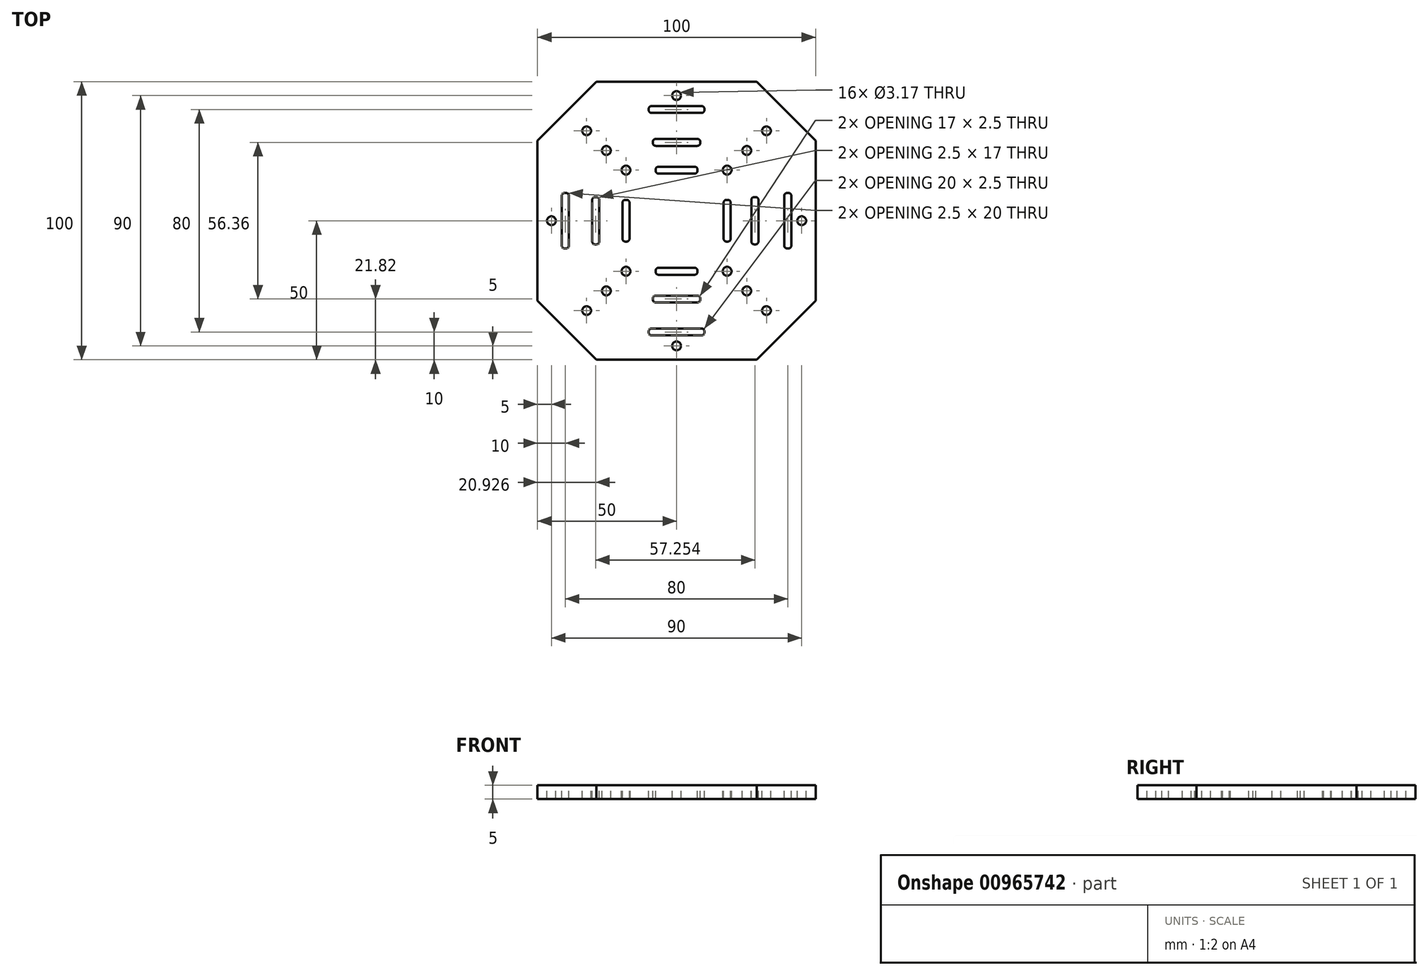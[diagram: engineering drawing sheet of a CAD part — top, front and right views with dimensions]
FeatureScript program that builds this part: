
annotation { "Feature Type Name" : "Feature", "Feature Type Description" : "" }
export const myFeature = defineFeature(function(context is Context, id is Id, definition is map)
    precondition{}
    {
        {
            var Q0;
            Q0=qCreatedBy(makeId("Top.planeOp"),FACE);
            var sketch = newSketch(context, id + "F0", { "sketchPlane" : qUnion([Q0])});
            skLineSegment(sketch, "E0.bottom", {"start": v(50, 50) * mm, "end": v(-50, 50) * mm});
            skLineSegment(sketch, "E0.top", {"start": v(50, -50) * mm, "end": v(-50, -50) * mm});
            skLineSegment(sketch, "E0.left", {"start": v(50, 50) * mm, "end": v(50, -50) * mm});
            skLineSegment(sketch, "E0.right", {"start": v(-50, 50) * mm, "end": v(-50, -50) * mm});
            skPoint(sketch, "E0.middle", {"position": v(0, 0) * mm});
            skSolve(sketch);
        }
        {
            var Q0;
            Q0=qSketchRegion(id+"F0",true);
            extrude(context, id + "F1", {"entities" : qUnion([Q0]), "depth" : 5 * mm, "offsetDistance" : 25 * mm});
        }
        {
            var Q0;
            Q0=makeQuery(id+"F1.opExtrude","SWEPT_EDGE",EDGE,{"disambiguationData":[OSD([sQuery(id+"F0.wireOp",EDGE,"E0.top"),sQuery(id+"F0.wireOp",EDGE,"E0.left")])]});
            var Q1;
            Q1=makeQuery(id+"F1.opExtrude","SWEPT_EDGE",EDGE,{"disambiguationData":[OSD([sQuery(id+"F0.wireOp",EDGE,"E0.bottom"),sQuery(id+"F0.wireOp",EDGE,"E0.left")])]});
            var Q2;
            Q2=makeQuery(id+"F1.opExtrude","SWEPT_EDGE",EDGE,{"disambiguationData":[OSD([sQuery(id+"F0.wireOp",EDGE,"E0.top"),sQuery(id+"F0.wireOp",EDGE,"E0.right")])]});
            var Q3;
            Q3=makeQuery(id+"F1.opExtrude","SWEPT_EDGE",EDGE,{"disambiguationData":[OSD([sQuery(id+"F0.wireOp",EDGE,"E0.bottom"),sQuery(id+"F0.wireOp",EDGE,"E0.right")])]});
            chamfer(context, id + "F2", {"entities" : qUnion([Q0, Q1, Q2, Q3]), "chamferType" : ChamferType.OFFSET_ANGLE, "width" : 21.21 * mm, "oppositeDirection" : false, "angle" : 45 * degree, "tangentPropagation" : true});
        }
        {
            var Q0;
            Q0=makeQuery(id+"F1.opExtrude","CAP_FACE",FACE,{"disambiguationData":[OSD([sQuery(id+"F0.wireOp",EDGE,"E0.bottom"),sQuery(id+"F0.wireOp",EDGE,"E0.top"),sQuery(id+"F0.wireOp",EDGE,"E0.left"),sQuery(id+"F0.wireOp",EDGE,"E0.right")])],"isStart":false});
            var sketch = newSketch(context, id + "F3", { "sketchPlane" : qUnion([Q0])});
            skLineSegment(sketch, "E1", {"start": v(-50, 28.79) * mm, "end": v(-14.64, -6.57) * mm});
            skLineSegment(sketch, "E2", {"start": v(-14.64, -6.57) * mm, "end": v(6.57, 14.64) * mm});
            skLineSegment(sketch, "E3", {"start": v(6.57, 14.64) * mm, "end": v(-28.79, 50) * mm});
            skCircle(sketch, "E4", {"center": v(-25.25, 25.25) * mm, "radius": 1.59 * mm});
            skLineSegment(sketch, "E5", {"start": v(-28.79, -50) * mm, "end": v(-0.5, -21.72) * mm});
            skLineSegment(sketch, "E6", {"start": v(-0.5, -21.72) * mm, "end": v(-21.72, -0.5) * mm});
            skLineSegment(sketch, "E7", {"start": v(-21.72, -0.5) * mm, "end": v(-50, -28.79) * mm});
            skLineSegment(sketch, "E8", {"start": v(50, -28.79) * mm, "end": v(14.64, 6.57) * mm});
            skLineSegment(sketch, "E9", {"start": v(14.64, 6.57) * mm, "end": v(-6.57, -14.64) * mm});
            skLineSegment(sketch, "E10", {"start": v(-6.57, -14.64) * mm, "end": v(28.79, -50) * mm});
            skLineSegment(sketch, "E11", {"start": v(28.79, 50) * mm, "end": v(0.5, 21.72) * mm});
            skLineSegment(sketch, "E12", {"start": v(0.5, 21.72) * mm, "end": v(21.72, 0.5) * mm});
            skLineSegment(sketch, "E13", {"start": v(21.72, 0.5) * mm, "end": v(50, 28.79) * mm});
            skCircle(sketch, "E14", {"center": v(-25.25, -25.25) * mm, "radius": 1.59 * mm});
            skCircle(sketch, "E15", {"center": v(25.25, -25.25) * mm, "radius": 1.59 * mm});
            skCircle(sketch, "E16", {"center": v(25.25, 25.25) * mm, "radius": 1.59 * mm});
            skCircle(sketch, "E17", {"center": v(-18.18, -18.18) * mm, "radius": 1.59 * mm});
            skCircle(sketch, "E18", {"center": v(18.18, -18.18) * mm, "radius": 1.59 * mm});
            skCircle(sketch, "E19", {"center": v(18.18, 18.18) * mm, "radius": 1.59 * mm});
            skCircle(sketch, "E20", {"center": v(-18.18, 18.18) * mm, "radius": 1.59 * mm});
            skCircle(sketch, "E21", {"center": v(-32.32, 32.32) * mm, "radius": 1.59 * mm});
            skCircle(sketch, "E22", {"center": v(-32.32, -32.32) * mm, "radius": 1.59 * mm});
            skCircle(sketch, "E23", {"center": v(32.32, -32.32) * mm, "radius": 1.59 * mm});
            skCircle(sketch, "E24", {"center": v(32.32, 32.32) * mm, "radius": 1.59 * mm});
            skPoint(sketch, "E25.middle", {"position": v(0, 40) * mm});
            skLineSegment(sketch, "E26.bottom", {"start": v(41.25, -10) * mm, "end": v(38.75, -10) * mm});
            skLineSegment(sketch, "E26.top", {"start": v(41.25, 10) * mm, "end": v(38.75, 10) * mm});
            skLineSegment(sketch, "E26.left", {"start": v(41.25, -10) * mm, "end": v(41.25, 10) * mm});
            skLineSegment(sketch, "E26.right", {"start": v(38.75, -10) * mm, "end": v(38.75, 10) * mm});
            skPoint(sketch, "E26.middle", {"position": v(40, 0) * mm});
            skLineSegment(sketch, "E27.bottom", {"start": v(-38.75, 10) * mm, "end": v(-41.25, 10) * mm});
            skLineSegment(sketch, "E27.top", {"start": v(-38.75, -10) * mm, "end": v(-41.25, -10) * mm});
            skLineSegment(sketch, "E27.left", {"start": v(-38.75, 10) * mm, "end": v(-38.75, -10) * mm});
            skLineSegment(sketch, "E27.right", {"start": v(-41.25, 10) * mm, "end": v(-41.25, -10) * mm});
            skPoint(sketch, "E27.middle", {"position": v(-40, 0) * mm});
            skLineSegment(sketch, "E28.bottom", {"start": v(10, -41.25) * mm, "end": v(-10, -41.25) * mm});
            skLineSegment(sketch, "E28.top", {"start": v(10, -38.75) * mm, "end": v(-10, -38.75) * mm});
            skLineSegment(sketch, "E28.left", {"start": v(10, -41.25) * mm, "end": v(10, -38.75) * mm});
            skLineSegment(sketch, "E28.right", {"start": v(-10, -41.25) * mm, "end": v(-10, -38.75) * mm});
            skPoint(sketch, "E28.middle", {"position": v(0, -40) * mm});
            skLineSegment(sketch, "E29.bottom", {"start": v(10, 41.25) * mm, "end": v(-10, 41.25) * mm});
            skLineSegment(sketch, "E29.top", {"start": v(10, 38.75) * mm, "end": v(-10, 38.75) * mm});
            skLineSegment(sketch, "E29.left", {"start": v(10, 41.25) * mm, "end": v(10, 38.75) * mm});
            skLineSegment(sketch, "E29.right", {"start": v(-10, 41.25) * mm, "end": v(-10, 38.75) * mm});
            skCircle(sketch, "E30", {"center": v(-45, 0) * mm, "radius": 1.59 * mm});
            skCircle(sketch, "E31", {"center": v(0, 45) * mm, "radius": 1.59 * mm});
            skCircle(sketch, "E32", {"center": v(0, -45) * mm, "radius": 1.59 * mm});
            skCircle(sketch, "E33", {"center": v(45, 0) * mm, "radius": 1.59 * mm});
            skSolve(sketch);
        }
        {
            var Q0;
            Q0=makeQuery(id+"F3.imprint","IMPRINT",FACE,{"disambiguationData":[TD([[makeQuery(id+"F3.imprint","IMPRINT",EDGE,{"derivedFrom":sQuery(id+"F3.wireOp",EDGE,"E4")}),1.0]])]});
            var Q1;
            Q1=makeQuery(id+"F3.imprint","IMPRINT",FACE,{"disambiguationData":[TD([[makeQuery(id+"F3.imprint","IMPRINT",EDGE,{"derivedFrom":sQuery(id+"F3.wireOp",EDGE,"E14")}),1.0]])]});
            var Q2;
            Q2=makeQuery(id+"F3.imprint","IMPRINT",FACE,{"disambiguationData":[TD([[makeQuery(id+"F3.imprint","IMPRINT",EDGE,{"derivedFrom":sQuery(id+"F3.wireOp",EDGE,"E15")}),1.0]])]});
            var Q3;
            Q3=makeQuery(id+"F3.imprint","IMPRINT",FACE,{"disambiguationData":[TD([[makeQuery(id+"F3.imprint","IMPRINT",EDGE,{"derivedFrom":sQuery(id+"F3.wireOp",EDGE,"E16")}),1.0]])]});
            var Q4;
            Q4=makeQuery(id+"F3.imprint","IMPRINT",FACE,{"disambiguationData":[TD([[makeQuery(id+"F3.imprint","IMPRINT",EDGE,{"derivedFrom":sQuery(id+"F3.wireOp",EDGE,"E17")}),1.0]])]});
            var Q5;
            Q5=makeQuery(id+"F3.imprint","IMPRINT",FACE,{"disambiguationData":[TD([[makeQuery(id+"F3.imprint","IMPRINT",EDGE,{"derivedFrom":sQuery(id+"F3.wireOp",EDGE,"E18")}),1.0]])]});
            var Q6;
            Q6=makeQuery(id+"F3.imprint","IMPRINT",FACE,{"disambiguationData":[TD([[makeQuery(id+"F3.imprint","IMPRINT",EDGE,{"derivedFrom":sQuery(id+"F3.wireOp",EDGE,"E19")}),1.0]])]});
            var Q7;
            Q7=makeQuery(id+"F3.imprint","IMPRINT",FACE,{"disambiguationData":[TD([[makeQuery(id+"F3.imprint","IMPRINT",EDGE,{"derivedFrom":sQuery(id+"F3.wireOp",EDGE,"E20")}),1.0]])]});
            var Q8;
            Q8=makeQuery(id+"F3.imprint","IMPRINT",FACE,{"disambiguationData":[TD([[makeQuery(id+"F3.imprint","IMPRINT",EDGE,{"derivedFrom":sQuery(id+"F3.wireOp",EDGE,"E22")}),1.0]])]});
            var Q9;
            Q9=makeQuery(id+"F3.imprint","IMPRINT",FACE,{"disambiguationData":[TD([[makeQuery(id+"F3.imprint","IMPRINT",EDGE,{"derivedFrom":sQuery(id+"F3.wireOp",EDGE,"E23")}),1.0]])]});
            var Q10;
            Q10=makeQuery(id+"F3.imprint","IMPRINT",FACE,{"disambiguationData":[TD([[makeQuery(id+"F3.imprint","IMPRINT",EDGE,{"derivedFrom":sQuery(id+"F3.wireOp",EDGE,"E24")}),1.0]])]});
            var Q11;
            Q11=makeQuery(id+"F3.imprint","IMPRINT",FACE,{"disambiguationData":[TD([[makeQuery(id+"F3.imprint","IMPRINT",EDGE,{"derivedFrom":sQuery(id+"F3.wireOp",EDGE,"E21")}),1.0]])]});
            var Q12;
            Q12=makeQuery(id+"F3.imprint","IMPRINT",FACE,{"disambiguationData":[TD([[makeQuery(id+"F3.imprint","IMPRINT",EDGE,{"derivedFrom":sQuery(id+"F3.wireOp",EDGE,"E27.bottom")}),1.0]])]});
            var Q13;
            Q13=makeQuery(id+"F3.imprint","IMPRINT",FACE,{"disambiguationData":[TD([[makeQuery(id+"F3.imprint","IMPRINT",EDGE,{"derivedFrom":sQuery(id+"F3.wireOp",EDGE,"E30")}),1.0]])]});
            var Q14;
            Q14=makeQuery(id+"F3.imprint","IMPRINT",FACE,{"disambiguationData":[TD([[makeQuery(id+"F3.imprint","IMPRINT",EDGE,{"derivedFrom":sQuery(id+"F3.wireOp",EDGE,"E28.bottom")}),-1.0]])]});
            var Q15;
            Q15=makeQuery(id+"F3.imprint","IMPRINT",FACE,{"disambiguationData":[TD([[makeQuery(id+"F3.imprint","IMPRINT",EDGE,{"derivedFrom":sQuery(id+"F3.wireOp",EDGE,"E32")}),1.0]])]});
            var Q16;
            Q16=makeQuery(id+"F3.imprint","IMPRINT",FACE,{"disambiguationData":[TD([[makeQuery(id+"F3.imprint","IMPRINT",EDGE,{"derivedFrom":sQuery(id+"F3.wireOp",EDGE,"E26.bottom")}),-1.0]])]});
            var Q17;
            Q17=makeQuery(id+"F3.imprint","IMPRINT",FACE,{"disambiguationData":[TD([[makeQuery(id+"F3.imprint","IMPRINT",EDGE,{"derivedFrom":sQuery(id+"F3.wireOp",EDGE,"E33")}),1.0]])]});
            var Q18;
            Q18=makeQuery(id+"F3.imprint","IMPRINT",FACE,{"disambiguationData":[TD([[makeQuery(id+"F3.imprint","IMPRINT",EDGE,{"derivedFrom":sQuery(id+"F3.wireOp",EDGE,"E31")}),1.0]])]});
            var Q19;
            Q19=makeQuery(id+"F3.imprint","IMPRINT",FACE,{"disambiguationData":[TD([[makeQuery(id+"F3.imprint","IMPRINT",EDGE,{"derivedFrom":sQuery(id+"F3.wireOp",EDGE,"E29.bottom")}),1.0]])]});
            extrude(context, id + "F4", {"entities" : qUnion([Q0, Q1, Q2, Q3, Q4, Q5, Q6, Q7, Q8, Q9, Q10, Q11, Q12, Q13, Q14, Q15, Q16, Q17, Q18, Q19]), "operationType" : NewBodyOperationType.REMOVE, "oppositeDirection" : true, "depth" : 5 * mm, "offsetDistance" : 25 * mm});
        }
        {
            var Q0;
            Q0=makeQuery(id+"F4.boolean.opBoolean","COPY",EDGE,{"derivedFrom":makeQuery(id+"F4.opExtrude","SWEPT_EDGE",EDGE,{"disambiguationData":[OSD([sQuery(id+"F3.wireOp",EDGE,"E27.bottom"),sQuery(id+"F3.wireOp",EDGE,"E27.right")])]})});
            var Q1;
            Q1=makeQuery(id+"F4.boolean.opBoolean","COPY",EDGE,{"derivedFrom":makeQuery(id+"F4.opExtrude","SWEPT_EDGE",EDGE,{"disambiguationData":[OSD([sQuery(id+"F3.wireOp",EDGE,"E28.top"),sQuery(id+"F3.wireOp",EDGE,"E28.right")])]})});
            var Q2;
            Q2=makeQuery(id+"F4.boolean.opBoolean","COPY",EDGE,{"derivedFrom":makeQuery(id+"F4.opExtrude","SWEPT_EDGE",EDGE,{"disambiguationData":[OSD([sQuery(id+"F3.wireOp",EDGE,"E26.top"),sQuery(id+"F3.wireOp",EDGE,"E26.right")])]})});
            var Q3;
            Q3=makeQuery(id+"F4.boolean.opBoolean","COPY",EDGE,{"derivedFrom":makeQuery(id+"F4.opExtrude","SWEPT_EDGE",EDGE,{"disambiguationData":[OSD([sQuery(id+"F3.wireOp",EDGE,"E29.bottom"),sQuery(id+"F3.wireOp",EDGE,"E29.right")])]})});
            var Q4;
            Q4=makeQuery(id+"F4.boolean.opBoolean","COPY",EDGE,{"derivedFrom":makeQuery(id+"F4.opExtrude","SWEPT_EDGE",EDGE,{"disambiguationData":[OSD([sQuery(id+"F3.wireOp",EDGE,"E28.top"),sQuery(id+"F3.wireOp",EDGE,"E28.left")])]})});
            var Q5;
            Q5=makeQuery(id+"F4.boolean.opBoolean","COPY",EDGE,{"derivedFrom":makeQuery(id+"F4.opExtrude","SWEPT_EDGE",EDGE,{"disambiguationData":[OSD([sQuery(id+"F3.wireOp",EDGE,"E26.top"),sQuery(id+"F3.wireOp",EDGE,"E26.left")])]})});
            var Q6;
            Q6=makeQuery(id+"F4.boolean.opBoolean","COPY",EDGE,{"derivedFrom":makeQuery(id+"F4.opExtrude","SWEPT_EDGE",EDGE,{"disambiguationData":[OSD([sQuery(id+"F3.wireOp",EDGE,"E27.bottom"),sQuery(id+"F3.wireOp",EDGE,"E27.left")])]})});
            var Q7;
            Q7=makeQuery(id+"F4.boolean.opBoolean","COPY",EDGE,{"derivedFrom":makeQuery(id+"F4.opExtrude","SWEPT_EDGE",EDGE,{"disambiguationData":[OSD([sQuery(id+"F3.wireOp",EDGE,"E29.bottom"),sQuery(id+"F3.wireOp",EDGE,"E29.left")])]})});
            var Q8;
            Q8=makeQuery(id+"F4.boolean.opBoolean","COPY",EDGE,{"derivedFrom":makeQuery(id+"F4.opExtrude","SWEPT_EDGE",EDGE,{"disambiguationData":[OSD([sQuery(id+"F3.wireOp",EDGE,"E26.bottom"),sQuery(id+"F3.wireOp",EDGE,"E26.left")])]})});
            var Q9;
            Q9=makeQuery(id+"F4.boolean.opBoolean","COPY",EDGE,{"derivedFrom":makeQuery(id+"F4.opExtrude","SWEPT_EDGE",EDGE,{"disambiguationData":[OSD([sQuery(id+"F3.wireOp",EDGE,"E28.bottom"),sQuery(id+"F3.wireOp",EDGE,"E28.left")])]})});
            var Q10;
            Q10=makeQuery(id+"F4.boolean.opBoolean","COPY",EDGE,{"derivedFrom":makeQuery(id+"F4.opExtrude","SWEPT_EDGE",EDGE,{"disambiguationData":[OSD([sQuery(id+"F3.wireOp",EDGE,"E29.top"),sQuery(id+"F3.wireOp",EDGE,"E29.left")])]})});
            var Q11;
            Q11=makeQuery(id+"F4.boolean.opBoolean","COPY",EDGE,{"derivedFrom":makeQuery(id+"F4.opExtrude","SWEPT_EDGE",EDGE,{"disambiguationData":[OSD([sQuery(id+"F3.wireOp",EDGE,"E27.top"),sQuery(id+"F3.wireOp",EDGE,"E27.left")])]})});
            var Q12;
            Q12=makeQuery(id+"F4.boolean.opBoolean","COPY",EDGE,{"derivedFrom":makeQuery(id+"F4.opExtrude","SWEPT_EDGE",EDGE,{"disambiguationData":[OSD([sQuery(id+"F3.wireOp",EDGE,"E29.top"),sQuery(id+"F3.wireOp",EDGE,"E29.right")])]})});
            var Q13;
            Q13=makeQuery(id+"F4.boolean.opBoolean","COPY",EDGE,{"derivedFrom":makeQuery(id+"F4.opExtrude","SWEPT_EDGE",EDGE,{"disambiguationData":[OSD([sQuery(id+"F3.wireOp",EDGE,"E26.bottom"),sQuery(id+"F3.wireOp",EDGE,"E26.right")])]})});
            var Q14;
            Q14=makeQuery(id+"F4.boolean.opBoolean","COPY",EDGE,{"derivedFrom":makeQuery(id+"F4.opExtrude","SWEPT_EDGE",EDGE,{"disambiguationData":[OSD([sQuery(id+"F3.wireOp",EDGE,"E27.top"),sQuery(id+"F3.wireOp",EDGE,"E27.right")])]})});
            var Q15;
            Q15=makeQuery(id+"F4.boolean.opBoolean","COPY",EDGE,{"derivedFrom":makeQuery(id+"F4.opExtrude","SWEPT_EDGE",EDGE,{"disambiguationData":[OSD([sQuery(id+"F3.wireOp",EDGE,"E28.bottom"),sQuery(id+"F3.wireOp",EDGE,"E28.right")])]})});
            fillet(context, id + "F5", {"entities" : qUnion([Q0, Q1, Q2, Q3, Q4, Q5, Q6, Q7, Q8, Q9, Q10, Q11, Q12, Q13, Q14, Q15]), "radius" : 1 * mm, "tangentPropagation" : true, "allowEdgeOverflow" : false});
        }
        {
            var Q0;
            Q0=makeQuery(id+"F1.opExtrude","CAP_FACE",FACE,{"disambiguationData":[OSD([sQuery(id+"F0.wireOp",EDGE,"E0.bottom"),sQuery(id+"F0.wireOp",EDGE,"E0.top"),sQuery(id+"F0.wireOp",EDGE,"E0.left"),sQuery(id+"F0.wireOp",EDGE,"E0.right")])],"isStart":false});
            var sketch = newSketch(context, id + "F6", { "sketchPlane" : qUnion([Q0])});
            skLineSegment(sketch, "E34", {"start": v(-18.18, 18.18) * mm, "end": v(-7.5, 18.18) * mm});
            skLineSegment(sketch, "E35.bottom", {"start": v(7.5, 19.43) * mm, "end": v(-7.5, 19.43) * mm});
            skLineSegment(sketch, "E35.top", {"start": v(7.5, 16.93) * mm, "end": v(-7.5, 16.93) * mm});
            skLineSegment(sketch, "E35.left", {"start": v(7.5, 19.43) * mm, "end": v(7.5, 16.93) * mm});
            skLineSegment(sketch, "E35.right", {"start": v(-7.5, 19.43) * mm, "end": v(-7.5, 16.93) * mm});
            skPoint(sketch, "E35.middle", {"position": v(0, 18.18) * mm});
            skLineSegment(sketch, "E36.bottom", {"start": v(-19.43, 7.5) * mm, "end": v(-16.93, 7.5) * mm});
            skLineSegment(sketch, "E36.top", {"start": v(-19.43, -7.5) * mm, "end": v(-16.93, -7.5) * mm});
            skLineSegment(sketch, "E36.left", {"start": v(-19.43, 7.5) * mm, "end": v(-19.43, -7.5) * mm});
            skLineSegment(sketch, "E36.right", {"start": v(-16.93, 7.5) * mm, "end": v(-16.93, -7.5) * mm});
            skPoint(sketch, "E36.middle", {"position": v(-18.18, 0) * mm});
            skLineSegment(sketch, "E37.bottom", {"start": v(7.5, -16.93) * mm, "end": v(-7.5, -16.93) * mm});
            skLineSegment(sketch, "E37.top", {"start": v(7.5, -19.43) * mm, "end": v(-7.5, -19.43) * mm});
            skLineSegment(sketch, "E37.left", {"start": v(7.5, -16.93) * mm, "end": v(7.5, -19.43) * mm});
            skLineSegment(sketch, "E37.right", {"start": v(-7.5, -16.93) * mm, "end": v(-7.5, -19.43) * mm});
            skPoint(sketch, "E37.middle", {"position": v(0, -18.18) * mm});
            skLineSegment(sketch, "E38.bottom", {"start": v(19.43, 7.5) * mm, "end": v(16.93, 7.5) * mm});
            skLineSegment(sketch, "E38.top", {"start": v(19.43, -7.5) * mm, "end": v(16.93, -7.5) * mm});
            skLineSegment(sketch, "E38.left", {"start": v(19.43, 7.5) * mm, "end": v(19.43, -7.5) * mm});
            skLineSegment(sketch, "E38.right", {"start": v(16.93, 7.5) * mm, "end": v(16.93, -7.5) * mm});
            skPoint(sketch, "E38.middle", {"position": v(18.18, 0) * mm});
            skLineSegment(sketch, "E39.bottom", {"start": v(-27.82, 8.5) * mm, "end": v(-30.32, 8.5) * mm});
            skLineSegment(sketch, "E39.top", {"start": v(-27.82, -8.5) * mm, "end": v(-30.32, -8.5) * mm});
            skLineSegment(sketch, "E39.left", {"start": v(-27.82, 8.5) * mm, "end": v(-27.82, -8.5) * mm});
            skLineSegment(sketch, "E39.right", {"start": v(-30.32, 8.5) * mm, "end": v(-30.32, -8.5) * mm});
            skPoint(sketch, "E39.middle", {"position": v(-29.07, 0) * mm});
            skLineSegment(sketch, "E40", {"start": v(0, 18.18) * mm, "end": v(0, 19.43) * mm});
            skLineSegment(sketch, "E41", {"start": v(0, -18.18) * mm, "end": v(0, -19.43) * mm});
            skLineSegment(sketch, "E42.bottom", {"start": v(8.5, -26.93) * mm, "end": v(-8.5, -26.93) * mm});
            skLineSegment(sketch, "E42.top", {"start": v(8.5, -29.43) * mm, "end": v(-8.5, -29.43) * mm});
            skLineSegment(sketch, "E42.left", {"start": v(8.5, -26.93) * mm, "end": v(8.5, -29.43) * mm});
            skLineSegment(sketch, "E42.right", {"start": v(-8.5, -26.93) * mm, "end": v(-8.5, -29.43) * mm});
            skPoint(sketch, "E42.middle", {"position": v(0, -28.18) * mm});
            skLineSegment(sketch, "E43.bottom", {"start": v(29.43, 8.5) * mm, "end": v(26.93, 8.5) * mm});
            skLineSegment(sketch, "E43.top", {"start": v(29.43, -8.5) * mm, "end": v(26.93, -8.5) * mm});
            skLineSegment(sketch, "E43.left", {"start": v(29.43, 8.5) * mm, "end": v(29.43, -8.5) * mm});
            skLineSegment(sketch, "E43.right", {"start": v(26.93, 8.5) * mm, "end": v(26.93, -8.5) * mm});
            skPoint(sketch, "E43.middle", {"position": v(28.18, 0) * mm});
            skLineSegment(sketch, "E44.bottom", {"start": v(8.5, 29.43) * mm, "end": v(-8.5, 29.43) * mm});
            skLineSegment(sketch, "E44.top", {"start": v(8.5, 26.93) * mm, "end": v(-8.5, 26.93) * mm});
            skLineSegment(sketch, "E44.left", {"start": v(8.5, 29.43) * mm, "end": v(8.5, 26.93) * mm});
            skLineSegment(sketch, "E44.right", {"start": v(-8.5, 29.43) * mm, "end": v(-8.5, 26.93) * mm});
            skPoint(sketch, "E44.middle", {"position": v(0, 28.18) * mm});
            skLineSegment(sketch, "E45.trimOffspring", {"start": v(-27.82, 0) * mm, "end": v(-29.07, 0) * mm});
            skPoint(sketch, "E46.orphan", {"position": v(-18.18, -18.18) * mm});
            skLineSegment(sketch, "E47.trimOffspring", {"start": v(0, -26.93) * mm, "end": v(0, -28.18) * mm});
            skLineSegment(sketch, "E48.trimOffspring", {"start": v(0, 26.93) * mm, "end": v(0, 28.18) * mm});
            skPoint(sketch, "E49.orphan", {"position": v(18.18, 18.18) * mm});
            skLineSegment(sketch, "E50.trimOffspring", {"start": v(26.93, 0) * mm, "end": v(28.18, 0) * mm});
            skPoint(sketch, "E51.end.orphan", {"position": v(18.18, -18.18) * mm});
            skSolve(sketch);
        }
        {
            var Q0;
            Q0=qSketchRegion(id+"F6",true);
            extrude(context, id + "F7", {"entities" : qUnion([Q0]), "operationType" : NewBodyOperationType.REMOVE, "oppositeDirection" : true, "depth" : 5 * mm, "offsetDistance" : 25 * mm});
        }
        {
            var Q0;
            Q0=makeQuery(id+"F7.boolean.opBoolean","COPY",EDGE,{"derivedFrom":makeQuery(id+"F7.opExtrude","SWEPT_EDGE",EDGE,{"disambiguationData":[OSD([sQuery(id+"F6.wireOp",EDGE,"E39.bottom"),sQuery(id+"F6.wireOp",EDGE,"E39.right")])]})});
            var Q1;
            Q1=makeQuery(id+"F7.boolean.opBoolean","COPY",EDGE,{"derivedFrom":makeQuery(id+"F7.opExtrude","SWEPT_EDGE",EDGE,{"disambiguationData":[OSD([sQuery(id+"F6.wireOp",EDGE,"E36.bottom"),sQuery(id+"F6.wireOp",EDGE,"E36.left")])]})});
            var Q2;
            Q2=makeQuery(id+"F7.boolean.opBoolean","COPY",EDGE,{"derivedFrom":makeQuery(id+"F7.opExtrude","SWEPT_EDGE",EDGE,{"disambiguationData":[OSD([sQuery(id+"F6.wireOp",EDGE,"E44.bottom"),sQuery(id+"F6.wireOp",EDGE,"E44.right")])]})});
            var Q3;
            Q3=makeQuery(id+"F7.boolean.opBoolean","COPY",EDGE,{"derivedFrom":makeQuery(id+"F7.opExtrude","SWEPT_EDGE",EDGE,{"disambiguationData":[OSD([sQuery(id+"F6.wireOp",EDGE,"E35.bottom"),sQuery(id+"F6.wireOp",EDGE,"E35.right")])]})});
            var Q4;
            Q4=makeQuery(id+"F7.boolean.opBoolean","COPY",EDGE,{"derivedFrom":makeQuery(id+"F7.opExtrude","SWEPT_EDGE",EDGE,{"disambiguationData":[OSD([sQuery(id+"F6.wireOp",EDGE,"E37.bottom"),sQuery(id+"F6.wireOp",EDGE,"E37.right")])]})});
            var Q5;
            Q5=makeQuery(id+"F7.boolean.opBoolean","COPY",EDGE,{"derivedFrom":makeQuery(id+"F7.opExtrude","SWEPT_EDGE",EDGE,{"disambiguationData":[OSD([sQuery(id+"F6.wireOp",EDGE,"E42.bottom"),sQuery(id+"F6.wireOp",EDGE,"E42.right")])]})});
            var Q6;
            Q6=makeQuery(id+"F7.boolean.opBoolean","COPY",EDGE,{"derivedFrom":makeQuery(id+"F7.opExtrude","SWEPT_EDGE",EDGE,{"disambiguationData":[OSD([sQuery(id+"F6.wireOp",EDGE,"E38.bottom"),sQuery(id+"F6.wireOp",EDGE,"E38.right")])]})});
            var Q7;
            Q7=makeQuery(id+"F7.boolean.opBoolean","COPY",EDGE,{"derivedFrom":makeQuery(id+"F7.opExtrude","SWEPT_EDGE",EDGE,{"disambiguationData":[OSD([sQuery(id+"F6.wireOp",EDGE,"E43.bottom"),sQuery(id+"F6.wireOp",EDGE,"E43.right")])]})});
            var Q8;
            Q8=makeQuery(id+"F7.boolean.opBoolean","COPY",EDGE,{"derivedFrom":makeQuery(id+"F7.opExtrude","SWEPT_EDGE",EDGE,{"disambiguationData":[OSD([sQuery(id+"F6.wireOp",EDGE,"E44.bottom"),sQuery(id+"F6.wireOp",EDGE,"E44.left")])]})});
            var Q9;
            Q9=makeQuery(id+"F7.boolean.opBoolean","COPY",EDGE,{"derivedFrom":makeQuery(id+"F7.opExtrude","SWEPT_EDGE",EDGE,{"disambiguationData":[OSD([sQuery(id+"F6.wireOp",EDGE,"E35.bottom"),sQuery(id+"F6.wireOp",EDGE,"E35.left")])]})});
            var Q10;
            Q10=makeQuery(id+"F7.boolean.opBoolean","COPY",EDGE,{"derivedFrom":makeQuery(id+"F7.opExtrude","SWEPT_EDGE",EDGE,{"disambiguationData":[OSD([sQuery(id+"F6.wireOp",EDGE,"E39.bottom"),sQuery(id+"F6.wireOp",EDGE,"E39.left")])]})});
            var Q11;
            Q11=makeQuery(id+"F7.boolean.opBoolean","COPY",EDGE,{"derivedFrom":makeQuery(id+"F7.opExtrude","SWEPT_EDGE",EDGE,{"disambiguationData":[OSD([sQuery(id+"F6.wireOp",EDGE,"E36.bottom"),sQuery(id+"F6.wireOp",EDGE,"E36.right")])]})});
            var Q12;
            Q12=makeQuery(id+"F7.boolean.opBoolean","COPY",EDGE,{"derivedFrom":makeQuery(id+"F7.opExtrude","SWEPT_EDGE",EDGE,{"disambiguationData":[OSD([sQuery(id+"F6.wireOp",EDGE,"E43.bottom"),sQuery(id+"F6.wireOp",EDGE,"E43.left")])]})});
            var Q13;
            Q13=makeQuery(id+"F7.boolean.opBoolean","COPY",EDGE,{"derivedFrom":makeQuery(id+"F7.opExtrude","SWEPT_EDGE",EDGE,{"disambiguationData":[OSD([sQuery(id+"F6.wireOp",EDGE,"E38.bottom"),sQuery(id+"F6.wireOp",EDGE,"E38.left")])]})});
            var Q14;
            Q14=makeQuery(id+"F7.boolean.opBoolean","COPY",EDGE,{"derivedFrom":makeQuery(id+"F7.opExtrude","SWEPT_EDGE",EDGE,{"disambiguationData":[OSD([sQuery(id+"F6.wireOp",EDGE,"E37.bottom"),sQuery(id+"F6.wireOp",EDGE,"E37.left")])]})});
            var Q15;
            Q15=makeQuery(id+"F7.boolean.opBoolean","COPY",EDGE,{"derivedFrom":makeQuery(id+"F7.opExtrude","SWEPT_EDGE",EDGE,{"disambiguationData":[OSD([sQuery(id+"F6.wireOp",EDGE,"E42.bottom"),sQuery(id+"F6.wireOp",EDGE,"E42.left")])]})});
            var Q16;
            Q16=makeQuery(id+"F7.boolean.opBoolean","COPY",EDGE,{"derivedFrom":makeQuery(id+"F7.opExtrude","SWEPT_EDGE",EDGE,{"disambiguationData":[OSD([sQuery(id+"F6.wireOp",EDGE,"E43.top"),sQuery(id+"F6.wireOp",EDGE,"E43.left")])]})});
            var Q17;
            Q17=makeQuery(id+"F7.boolean.opBoolean","COPY",EDGE,{"derivedFrom":makeQuery(id+"F7.opExtrude","SWEPT_EDGE",EDGE,{"disambiguationData":[OSD([sQuery(id+"F6.wireOp",EDGE,"E38.top"),sQuery(id+"F6.wireOp",EDGE,"E38.left")])]})});
            var Q18;
            Q18=makeQuery(id+"F7.boolean.opBoolean","COPY",EDGE,{"derivedFrom":makeQuery(id+"F7.opExtrude","SWEPT_EDGE",EDGE,{"disambiguationData":[OSD([sQuery(id+"F6.wireOp",EDGE,"E37.top"),sQuery(id+"F6.wireOp",EDGE,"E37.left")])]})});
            var Q19;
            Q19=makeQuery(id+"F7.boolean.opBoolean","COPY",EDGE,{"derivedFrom":makeQuery(id+"F7.opExtrude","SWEPT_EDGE",EDGE,{"disambiguationData":[OSD([sQuery(id+"F6.wireOp",EDGE,"E42.top"),sQuery(id+"F6.wireOp",EDGE,"E42.left")])]})});
            var Q20;
            Q20=makeQuery(id+"F7.boolean.opBoolean","COPY",EDGE,{"derivedFrom":makeQuery(id+"F7.opExtrude","SWEPT_EDGE",EDGE,{"disambiguationData":[OSD([sQuery(id+"F6.wireOp",EDGE,"E35.top"),sQuery(id+"F6.wireOp",EDGE,"E35.left")])]})});
            var Q21;
            Q21=makeQuery(id+"F7.boolean.opBoolean","COPY",EDGE,{"derivedFrom":makeQuery(id+"F7.opExtrude","SWEPT_EDGE",EDGE,{"disambiguationData":[OSD([sQuery(id+"F6.wireOp",EDGE,"E44.top"),sQuery(id+"F6.wireOp",EDGE,"E44.left")])]})});
            var Q22;
            Q22=makeQuery(id+"F7.boolean.opBoolean","COPY",EDGE,{"derivedFrom":makeQuery(id+"F7.opExtrude","SWEPT_EDGE",EDGE,{"disambiguationData":[OSD([sQuery(id+"F6.wireOp",EDGE,"E39.top"),sQuery(id+"F6.wireOp",EDGE,"E39.left")])]})});
            var Q23;
            Q23=makeQuery(id+"F7.boolean.opBoolean","COPY",EDGE,{"derivedFrom":makeQuery(id+"F7.opExtrude","SWEPT_EDGE",EDGE,{"disambiguationData":[OSD([sQuery(id+"F6.wireOp",EDGE,"E36.top"),sQuery(id+"F6.wireOp",EDGE,"E36.right")])]})});
            var Q24;
            Q24=makeQuery(id+"F7.boolean.opBoolean","COPY",EDGE,{"derivedFrom":makeQuery(id+"F7.opExtrude","SWEPT_EDGE",EDGE,{"disambiguationData":[OSD([sQuery(id+"F6.wireOp",EDGE,"E37.top"),sQuery(id+"F6.wireOp",EDGE,"E37.right")])]})});
            var Q25;
            Q25=makeQuery(id+"F7.boolean.opBoolean","COPY",EDGE,{"derivedFrom":makeQuery(id+"F7.opExtrude","SWEPT_EDGE",EDGE,{"disambiguationData":[OSD([sQuery(id+"F6.wireOp",EDGE,"E42.top"),sQuery(id+"F6.wireOp",EDGE,"E42.right")])]})});
            var Q26;
            Q26=makeQuery(id+"F7.boolean.opBoolean","COPY",EDGE,{"derivedFrom":makeQuery(id+"F7.opExtrude","SWEPT_EDGE",EDGE,{"disambiguationData":[OSD([sQuery(id+"F6.wireOp",EDGE,"E39.top"),sQuery(id+"F6.wireOp",EDGE,"E39.right")])]})});
            var Q27;
            Q27=makeQuery(id+"F7.boolean.opBoolean","COPY",EDGE,{"derivedFrom":makeQuery(id+"F7.opExtrude","SWEPT_EDGE",EDGE,{"disambiguationData":[OSD([sQuery(id+"F6.wireOp",EDGE,"E36.top"),sQuery(id+"F6.wireOp",EDGE,"E36.left")])]})});
            var Q28;
            Q28=makeQuery(id+"F7.boolean.opBoolean","COPY",EDGE,{"derivedFrom":makeQuery(id+"F7.opExtrude","SWEPT_EDGE",EDGE,{"disambiguationData":[OSD([sQuery(id+"F6.wireOp",EDGE,"E38.top"),sQuery(id+"F6.wireOp",EDGE,"E38.right")])]})});
            var Q29;
            Q29=makeQuery(id+"F7.boolean.opBoolean","COPY",EDGE,{"derivedFrom":makeQuery(id+"F7.opExtrude","SWEPT_EDGE",EDGE,{"disambiguationData":[OSD([sQuery(id+"F6.wireOp",EDGE,"E43.top"),sQuery(id+"F6.wireOp",EDGE,"E43.right")])]})});
            var Q30;
            Q30=makeQuery(id+"F7.boolean.opBoolean","COPY",EDGE,{"derivedFrom":makeQuery(id+"F7.opExtrude","SWEPT_EDGE",EDGE,{"disambiguationData":[OSD([sQuery(id+"F6.wireOp",EDGE,"E44.top"),sQuery(id+"F6.wireOp",EDGE,"E44.right")])]})});
            var Q31;
            Q31=makeQuery(id+"F7.boolean.opBoolean","COPY",EDGE,{"derivedFrom":makeQuery(id+"F7.opExtrude","SWEPT_EDGE",EDGE,{"disambiguationData":[OSD([sQuery(id+"F6.wireOp",EDGE,"E35.top"),sQuery(id+"F6.wireOp",EDGE,"E35.right")])]})});
            fillet(context, id + "F8", {"entities" : qUnion([Q0, Q1, Q2, Q3, Q4, Q5, Q6, Q7, Q8, Q9, Q10, Q11, Q12, Q13, Q14, Q15, Q16, Q17, Q18, Q19, Q20, Q21, Q22, Q23, Q24, Q25, Q26, Q27, Q28, Q29, Q30, Q31]), "radius" : 1 * mm, "tangentPropagation" : true, "allowEdgeOverflow" : false});
        }
    });
